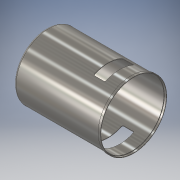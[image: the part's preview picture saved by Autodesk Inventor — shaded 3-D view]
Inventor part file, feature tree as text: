
AUTODESK INVENTOR PART (.ipt)
format: ipt  version: 2016 (Build 200138000, 138)  size: 199,680 bytes
history: native  units: in
note: dims shown in document units (in); Inventor stores cm internally (conversion verified against a paired STEP export)
features: extrude x5, sketch x4, fillet x1, shell x1
ambient origin geometry x8: Origin, YZ Plane, XZ Plane, XY Plane, X Axis, Y Axis, Z Axis, Center Point
bodies: Solid1 (feature_tree)
feature tree (11):
  extrude  "Extrusion1"  Depth=1.875in TaperAngle=0.0deg
  fillet  "Fillet1"  Radius=0.05in
  sketch  "Sketch2"  dims[d4=0.625in d5=0.25in d6=0.3in]
  extrude  "Extrusion3"  Depth=0.25in
  shell  "Shell2"  Thickness=0.3in
  extrude  "Extrusion2"  Depth=1.875in TaperAngle=0.0deg
  extrude  "Extrusion4"  Depth=0.025in TaperAngle=0.0deg
  extrude  "Extrusion5"  Depth=0.025in
  sketch  "Sketch1"  dims[d0=1.4in d1=1.875in d2=0.0in d3=0.05in]
  sketch  "Sketch3"  dims[d7=0.3875in d9=1.875in d10=0.0in]
  sketch  "Sketch4"  dims[d11=1.425in d12=0.05in d13=0.0in d14=0.025in d15=0.01in d16=0.375in d17=0.05in d18=0.0in d19=1.0in d20=0.0in]
